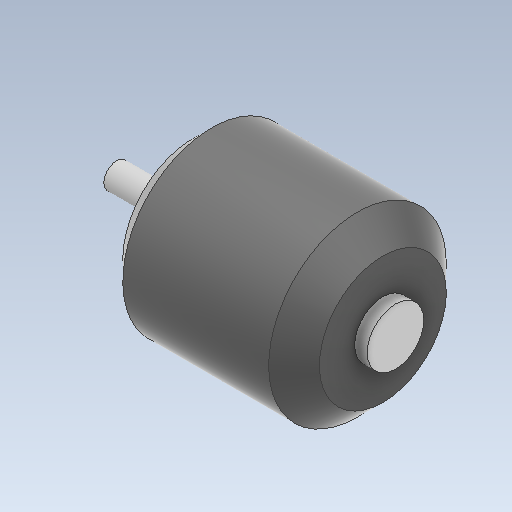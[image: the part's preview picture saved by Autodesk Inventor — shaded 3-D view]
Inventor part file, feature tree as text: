
AUTODESK INVENTOR PART (.ipt)
format: ipt  version: 2020 (Build 240168000, 168)  size: 176,640 bytes
history: native  units: mm
features: extrude x7, sketch x6, chamfer x2, other x1
ambient origin geometry x8: Origin, YZ Plane, XZ Plane, XY Plane, X Axis, Y Axis, Z Axis, Center Point
bodies: Body1 (feature_tree)
feature tree (16):
  other  "Твердое тело1"
  extrude  "Выдавливание1"  Depth=28.0mm
  extrude  "Выдавливание2"  Depth=18.0mm TaperAngle=0.0deg
  chamfer  "Фаска1"  Distance=28.0mm
  extrude  "Выдавливание3"  Depth=6.0mm TaperAngle=0.0deg
  extrude  "Выдавливание4"  Depth=2.0mm TaperAngle=45.0deg
  chamfer  "Фаска2"  Distance=8.9mm
  extrude  "Выдавливание5"  Depth=2.0mm TaperAngle=0.0deg
  extrude  "Выдавливание6"  Depth=28.0mm
  extrude  "Выдавливание7"  Depth=6.0mm TaperAngle=0.0deg
  sketch  "Эскиз1"
  sketch  "Эскиз2"
  sketch  "Эскиз3"
  sketch  "Эскиз4"
  sketch  "Эскиз5"
  sketch  "Эскиз6"
